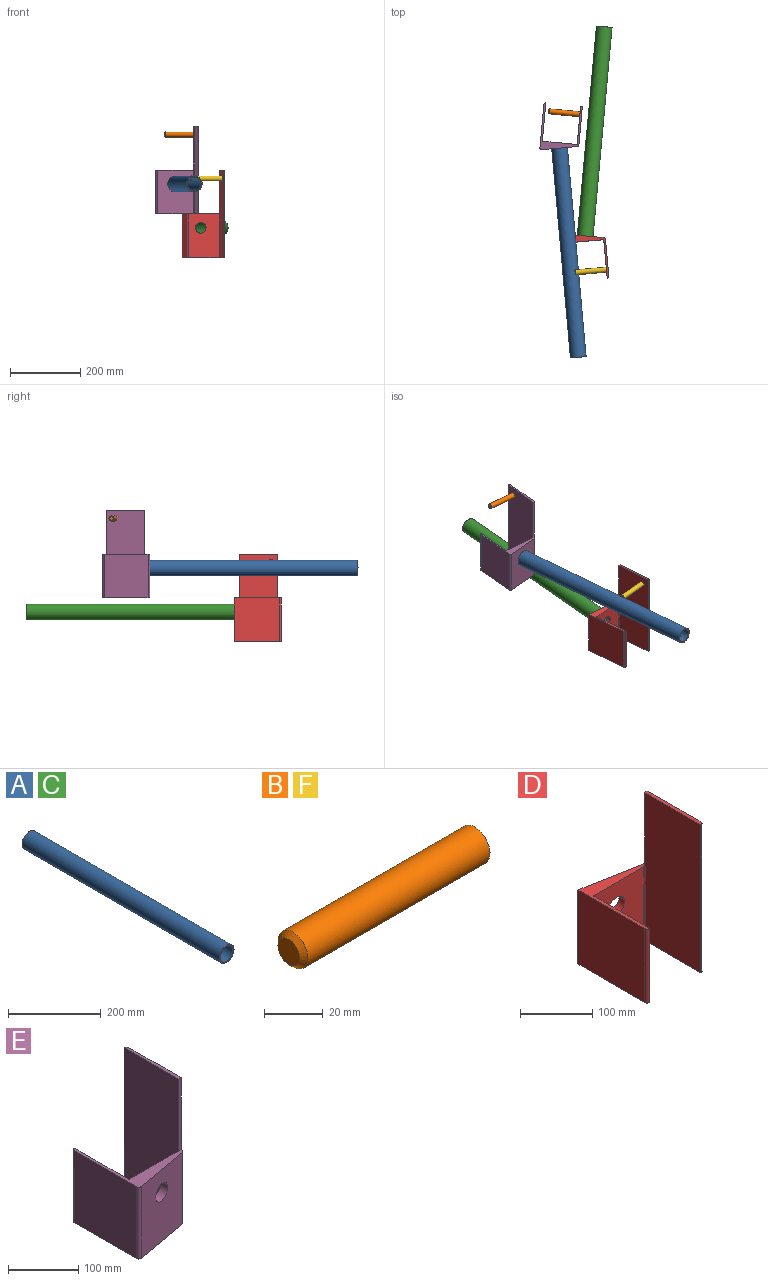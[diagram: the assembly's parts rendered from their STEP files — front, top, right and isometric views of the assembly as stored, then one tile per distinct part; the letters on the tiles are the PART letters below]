
ASSEMBLY  parts=6 mates=4
PART A: 4 faces, bbox 45x600x45 mm
  f0: cylinder r=19.5mm len=600mm, axis (0,1,0), area 73513.3mm2, adj f2,f3
  f1: cylinder r=22.5mm len=600mm, axis (0,1,0), area 84823mm2, adj f2,f3
  f2: plane 45x45mm, normal (0,-1,0), area 395.8mm2, adj f0,f1
  f3: plane 45x45mm, normal (0,1,0), area 395.8mm2, adj f0,f1
PART B: 4 faces, bbox 90x14.5x14.5 mm
  f0: cylinder r=7.25mm len=88mm, axis (-1,0,0), area 4008.7mm2, adj f1,f3
  f1: plane 14.5x14.5mm, normal (1,0,0), area 165.1mm2, adj f0
  f2: plane 10.5x10.5mm, normal (-1,0,0), area 86.6mm2, adj f3
  f3: cone r=7.25mm half-angle=45deg, axis (1,0,0), area 111.1mm2, adj f0,f2
PART C: same geometry as A
PART D: 18 faces, bbox 111.1x136.1x251.1 mm
  f0: plane 110x5mm, normal (0,0,1), area 545.7mm2, adj f1,f5,f9,f13,f16
  f1: plane 250x106.74mm, normal (1,0,0), area 26530.6mm2, adj f0,f3,f10,f11,f13,f16
  f2: plane 125x106.31mm, normal (0.18,0.98,0), area 12799.1mm2, adj f3,f6,f10,f11,f17
  f3: cylinder r=4.5mm len=125mm, axis (0,0,1), area 782.4mm2, adj f1,f2,f10,f11
  f4: plane 125x0.5mm, normal (0,-1,0), area 62.5mm2, adj f7,f10,f11,f12
  f5: plane 250x0.5mm, normal (0,-1,0), area 125mm2, adj f0,f9,f10,f13
  f6: plane 130.5x125mm, normal (-1,0,0), area 16312.5mm2, adj f2,f10,f11,f12
  f7: plane 125x108.5mm, normal (1,0,0), area 13562.5mm2, adj f4,f10,f11,f14
  f8: plane 126.15x98.15mm, normal (0,-1,0), area 11406.6mm2, adj f10,f11,f14,f15,f17
  f9: plane 250x110mm, normal (-1,0,0), area 27312.5mm2, adj f0,f5,f10,f11,f15,f16
  f10: plane 135x110mm, normal (0,0,-1), area 2739.5mm2, adj f1,f2,f3,f4,f5,f6,f7,f8
  f11: plane 135x110mm, normal (0,0,1), area 2193.8mm2, adj f1,f2,f3,f4,f6,f7,f8,f9
  f12: cylinder r=4.5mm len=125mm, axis (0,0,1), area 883.6mm2, adj f4,f6,f10,f11
  f13: cylinder r=4.5mm len=250mm, axis (0,0,-1), area 1767.1mm2, adj f0,f1,f5,f10
  f14: cylinder r=1.5mm len=125mm, axis (0,0,-1), area 294.5mm2, adj f7,f8,f10,f11
  f15: cylinder r=1.5mm len=125mm, axis (0,0,1), area 294.5mm2, adj f8,f9,f10,f11
  f16: plane 125x5mm, normal (0,1,0), area 625mm2, adj f0,f1,f9,f11
  f17: cylinder r=15mm len=32.79mm, axis (0.18,0.98,0), area 1469.1mm2, adj f2,f8
PART E: 19 faces, bbox 110x134.1x250 mm
  f0: plane 250x110mm, normal (-1,0,0), area 27312.5mm2, adj f1,f8,f9,f10,f15,f17
  f1: plane 250x0.5mm, normal (0,1,0), area 125mm2, adj f0,f8,f9,f14
  f2: plane 125.11x125mm, normal (-1,0,0), area 15638.5mm2, adj f9,f10,f11,f12
  f3: plane 125x0.5mm, normal (0,1,0), area 62.5mm2, adj f5,f9,f10,f11
  f4: plane 125x101mm, normal (0.18,-0.98,0), area 12125.1mm2, adj f9,f10,f12,f13,f18
  f5: plane 125x108.5mm, normal (1,0,0), area 13562.5mm2, adj f3,f9,f10,f16
  f6: plane 125x97mm, normal (0,1,0), area 11406.6mm2, adj f9,f10,f15,f16,f18
  f7: plane 250x106.74mm, normal (1,0,0), area 26530.6mm2, adj f8,f9,f10,f13,f14,f17
  f8: plane 110x5mm, normal (0,0,1), area 545.7mm2, adj f0,f1,f7,f14,f17
  f9: plane 134.11x110mm, normal (0,0,-1), area 2732.9mm2, adj f0,f1,f2,f3,f4,f5,f6,f7
  f10: plane 134.11x110mm, normal (0,0,1), area 2187.3mm2, adj f0,f2,f3,f4,f5,f6,f7,f11
  f11: cylinder r=4.5mm len=125mm, axis (0,0,-1), area 883.6mm2, adj f2,f3,f9,f10
  f12: cylinder r=4.5mm len=125mm, axis (0,0,1), area 984.7mm2, adj f2,f4,f9,f10
  f13: cylinder r=4.5mm len=125mm, axis (0,0,-1), area 782.4mm2, adj f4,f7,f9,f10
  f14: cylinder r=4.5mm len=250mm, axis (0,0,1), area 1767.1mm2, adj f1,f7,f8,f9
  f15: cylinder r=1.5mm len=125mm, axis (0,0,-1), area 294.5mm2, adj f0,f6,f9,f10
  f16: cylinder r=1.5mm len=125mm, axis (0,0,1), area 294.5mm2, adj f5,f6,f9,f10
  f17: plane 125x5mm, normal (0,-1,0), area 625mm2, adj f0,f7,f8,f10
  f18: cylinder r=15mm len=32.71mm, axis (0.18,-0.98,0), area 1422.9mm2, adj f4,f6
PART F: same geometry as B
PLACE A rot(axis=(0,0,1),5.1deg) t=(136.21,161.57,18.79)mm
PLACE B rot(axis=(0,0,-1),5.2deg) t=(-258.55,599.77,-58.26)mm
PLACE C rot(axis=(0,0,-1),5.2deg) t=(263.72,436.85,-106.31)mm
PLACE D rot(axis=(0,0,1),5.1deg) t=(64.2,-112.49,-237.93)mm
PLACE E rot(axis=(0,0,-1),5.2deg) t=(-1.33,227.88,-112.84)mm
PLACE F rot(axis=(0,0,1),5.1deg) t=(-249.34,139.71,-183.81)mm
MATE fastened E.f18 <-> A.f0  axis (0.09,-1,0) through (-260.64,126.08,-27.84)mm
MATE fastened B.f0 <-> E.f0  axis (1,-0.09,0) through (-202.45,222.76,113.86)mm
MATE fastened F.f0 <-> D.f9  axis (1,0.09,0) through (-126.71,-221.18,-11.68)mm
MATE fastened C.f0 <-> D.f17  axis (-0.09,-1,0) through (-187.4,-124.62,-152.93)mm
